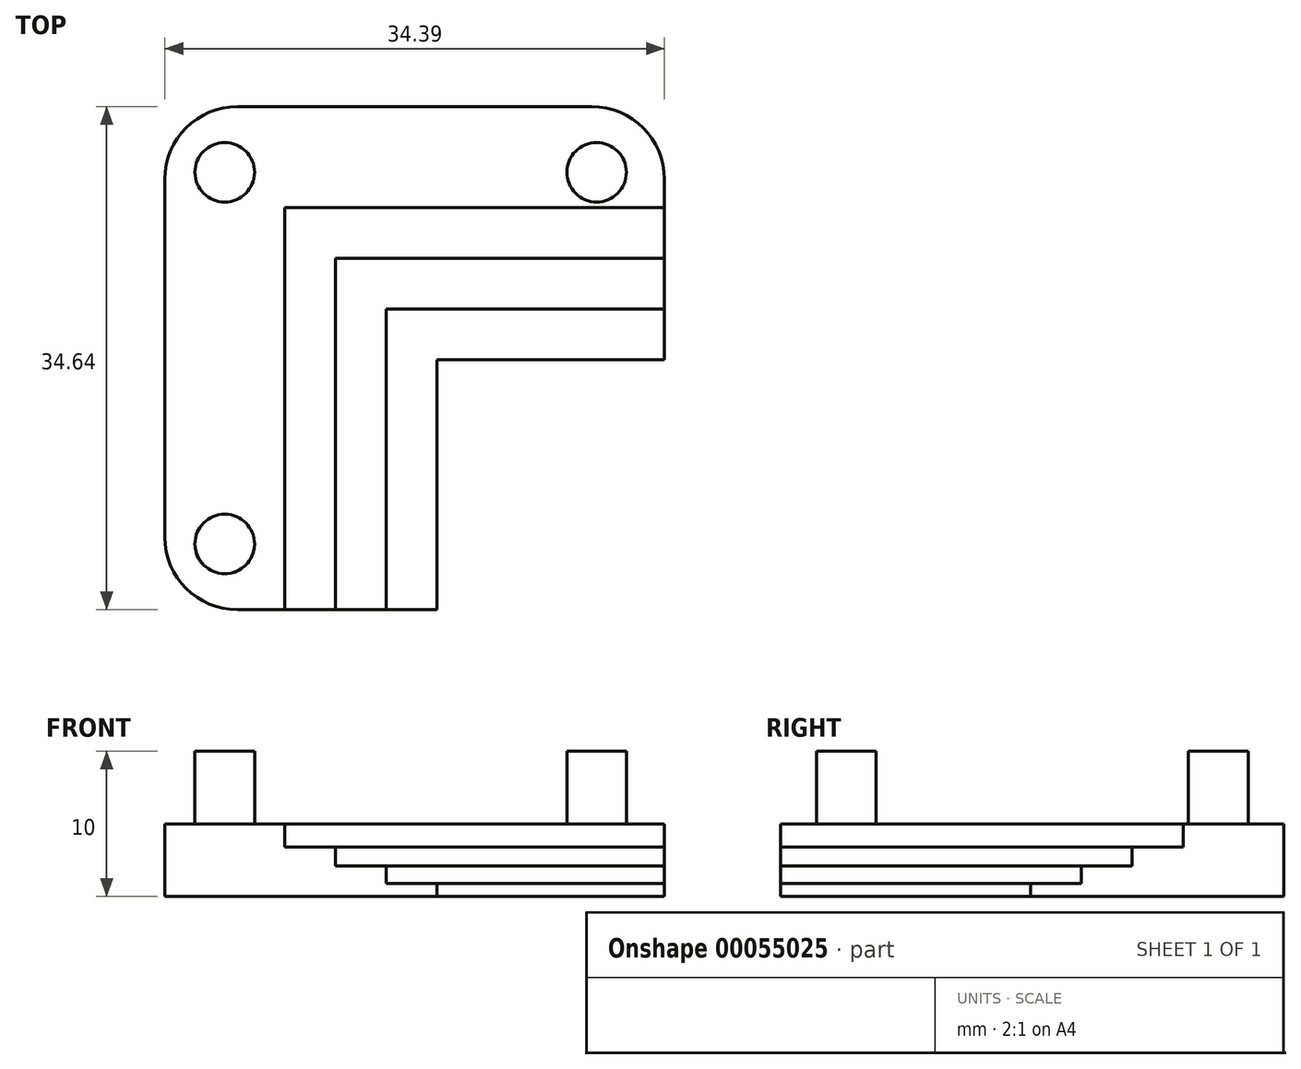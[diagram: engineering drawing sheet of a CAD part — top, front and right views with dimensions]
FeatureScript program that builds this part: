
annotation { "Feature Type Name" : "Feature", "Feature Type Description" : "" }
export const myFeature = defineFeature(function(context is Context, id is Id, definition is map)
    precondition{}
    {
        {
            var Q0;
            Q0=qCreatedBy(makeId("Top.planeOp"),FACE);
            var sketch = newSketch(context, id + "F0", { "sketchPlane" : qUnion([Q0])});
            skCircle(sketch, "E0", {"center": v(0, 0) * mm, "radius": 2.05 * mm});
            skLineSegment(sketch, "E1", {"start": v(0, 0) * mm, "end": v(0, -25.6) * mm});
            skCircle(sketch, "E2", {"center": v(0, -25.6) * mm, "radius": 2.05 * mm});
            skLineSegment(sketch, "E3.rect.bottom", {"start": v(-4.12, -30.12) * mm, "end": v(4.12, -30.12) * mm});
            skLineSegment(sketch, "E3.rect.top", {"start": v(-4.12, 4.52) * mm, "end": v(4.12, 4.52) * mm});
            skLineSegment(sketch, "E3.rect.left", {"start": v(-4.12, -30.12) * mm, "end": v(-4.12, 4.52) * mm});
            skLineSegment(sketch, "E3.rect.right", {"start": v(4.12, -30.12) * mm, "end": v(4.12, -2.42) * mm});
            skPoint(sketch, "E3.rect.middle", {"position": v(0, -12.8) * mm});
            skLineSegment(sketch, "E4", {"start": v(0, 0) * mm, "end": v(25.6, 0) * mm});
            skCircle(sketch, "E5", {"center": v(25.6, 0) * mm, "radius": 2.05 * mm});
            skLineSegment(sketch, "E6", {"start": v(4.12, 4.52) * mm, "end": v(30.27, 4.52) * mm});
            skLineSegment(sketch, "E7", {"start": v(30.27, 4.52) * mm, "end": v(30.27, -2.42) * mm});
            skLineSegment(sketch, "E8", {"start": v(30.27, -2.42) * mm, "end": v(4.12, -2.42) * mm});
            skLineSegment(sketch, "E9", {"start": v(30.27, -2.42) * mm, "end": v(30.27, -5.92) * mm});
            skLineSegment(sketch, "E10", {"start": v(30.27, -5.92) * mm, "end": v(30.27, -9.42) * mm});
            skLineSegment(sketch, "E11", {"start": v(30.27, -9.42) * mm, "end": v(30.27, -12.92) * mm});
            skLineSegment(sketch, "E12", {"start": v(4.12, -30.12) * mm, "end": v(7.62, -30.12) * mm});
            skLineSegment(sketch, "E13", {"start": v(7.62, -30.12) * mm, "end": v(11.12, -30.12) * mm});
            skLineSegment(sketch, "E14", {"start": v(11.12, -30.12) * mm, "end": v(14.62, -30.12) * mm});
            skLineSegment(sketch, "E15", {"start": v(30.27, -12.92) * mm, "end": v(14.62, -12.92) * mm});
            skLineSegment(sketch, "E16", {"start": v(14.62, -12.92) * mm, "end": v(14.62, -30.12) * mm});
            skLineSegment(sketch, "E17", {"start": v(11.12, -30.12) * mm, "end": v(11.12, -9.42) * mm});
            skLineSegment(sketch, "E18", {"start": v(11.12, -9.42) * mm, "end": v(30.27, -9.42) * mm});
            skLineSegment(sketch, "E19", {"start": v(30.27, -5.92) * mm, "end": v(7.62, -5.92) * mm});
            skLineSegment(sketch, "E20", {"start": v(7.62, -5.92) * mm, "end": v(7.62, -30.12) * mm});
            skSolve(sketch);
        }
        {
            var Q0;
            Q0=makeQuery(id+"F0.imprint","IMPRINT",FACE,{"disambiguationData":[TD([[makeQuery(id+"F0.imprint","IMPRINT",EDGE,{"derivedFrom":sQuery(id+"F0.wireOp",EDGE,"E2")}),-1.0]])]});
            extrude(context, id + "F1", {"entities" : qUnion([Q0]), "depth" : 5 * mm});
        }
        {
            var Q0;
            Q0=qCreatedBy(makeId("Top.planeOp"),FACE);
            var sketch = newSketch(context, id + "F2", { "sketchPlane" : qUnion([Q0])});
            skCircle(sketch, "E21", {"center": v(0, 0) * mm, "radius": 2.05 * mm});
            skCircle(sketch, "E22", {"center": v(0, -25.6) * mm, "radius": 2.05 * mm});
            skLineSegment(sketch, "E23", {"start": v(0, 0) * mm, "end": v(25.6, 0) * mm});
            skCircle(sketch, "E24", {"center": v(25.6, 0) * mm, "radius": 2.05 * mm});
            skSolve(sketch);
        }
        {
            var Q0;
            Q0=qSketchRegion(id+"F2",true);
            extrude(context, id + "F3", {"entities" : qUnion([Q0]), "operationType" : NewBodyOperationType.ADD, "depth" : 10 * mm});
        }
        {
            var Q0;
            Q0=makeQuery(id+"F1.opExtrude","SWEPT_EDGE",EDGE,{"disambiguationData":[OSD([sQuery(id+"F0.wireOp",EDGE,"E6"),sQuery(id+"F0.wireOp",EDGE,"E7")])]});
            var Q1;
            Q1=makeQuery(id+"F1.opExtrude","SWEPT_EDGE",EDGE,{"disambiguationData":[OSD([sQuery(id+"F0.wireOp",EDGE,"E3.rect.top"),sQuery(id+"F0.wireOp",EDGE,"E3.rect.left")])]});
            var Q2;
            Q2=makeQuery(id+"F1.opExtrude","SWEPT_EDGE",EDGE,{"disambiguationData":[OSD([sQuery(id+"F0.wireOp",EDGE,"E3.rect.bottom"),sQuery(id+"F0.wireOp",EDGE,"E3.rect.left")])]});
            fillet(context, id + "F4", {"entities" : qUnion([Q0, Q1, Q2]), "radius" : 5 * mm, "tangentPropagation" : true, "allowEdgeOverflow" : false});
        }
        {
            var Q0;
            Q0=makeQuery(id+"F0.imprint","IMPRINT",FACE,{"disambiguationData":[TD([[makeQuery(id+"F0.imprint","IMPRINT",EDGE,{"derivedFrom":sQuery(id+"F0.wireOp",EDGE,"E3.rect.right")}),-1.0]])]});
            extrude(context, id + "F5", {"entities" : qUnion([Q0]), "operationType" : NewBodyOperationType.ADD, "depth" : 3.4 * mm});
        }
        {
            var Q0;
            Q0=makeQuery(id+"F0.imprint","IMPRINT",FACE,{"disambiguationData":[TD([[makeQuery(id+"F0.imprint","IMPRINT",EDGE,{"derivedFrom":sQuery(id+"F0.wireOp",EDGE,"E10")}),-1.0]])]});
            extrude(context, id + "F6", {"entities" : qUnion([Q0]), "operationType" : NewBodyOperationType.ADD, "depth" : 2.1 * mm});
        }
        {
            var Q0;
            Q0=makeQuery(id+"F0.imprint","IMPRINT",FACE,{"disambiguationData":[TD([[makeQuery(id+"F0.imprint","IMPRINT",EDGE,{"derivedFrom":sQuery(id+"F0.wireOp",EDGE,"E11")}),-1.0]])]});
            extrude(context, id + "F7", {"entities" : qUnion([Q0]), "operationType" : NewBodyOperationType.ADD, "depth" : 0.9 * mm});
        }
    });
